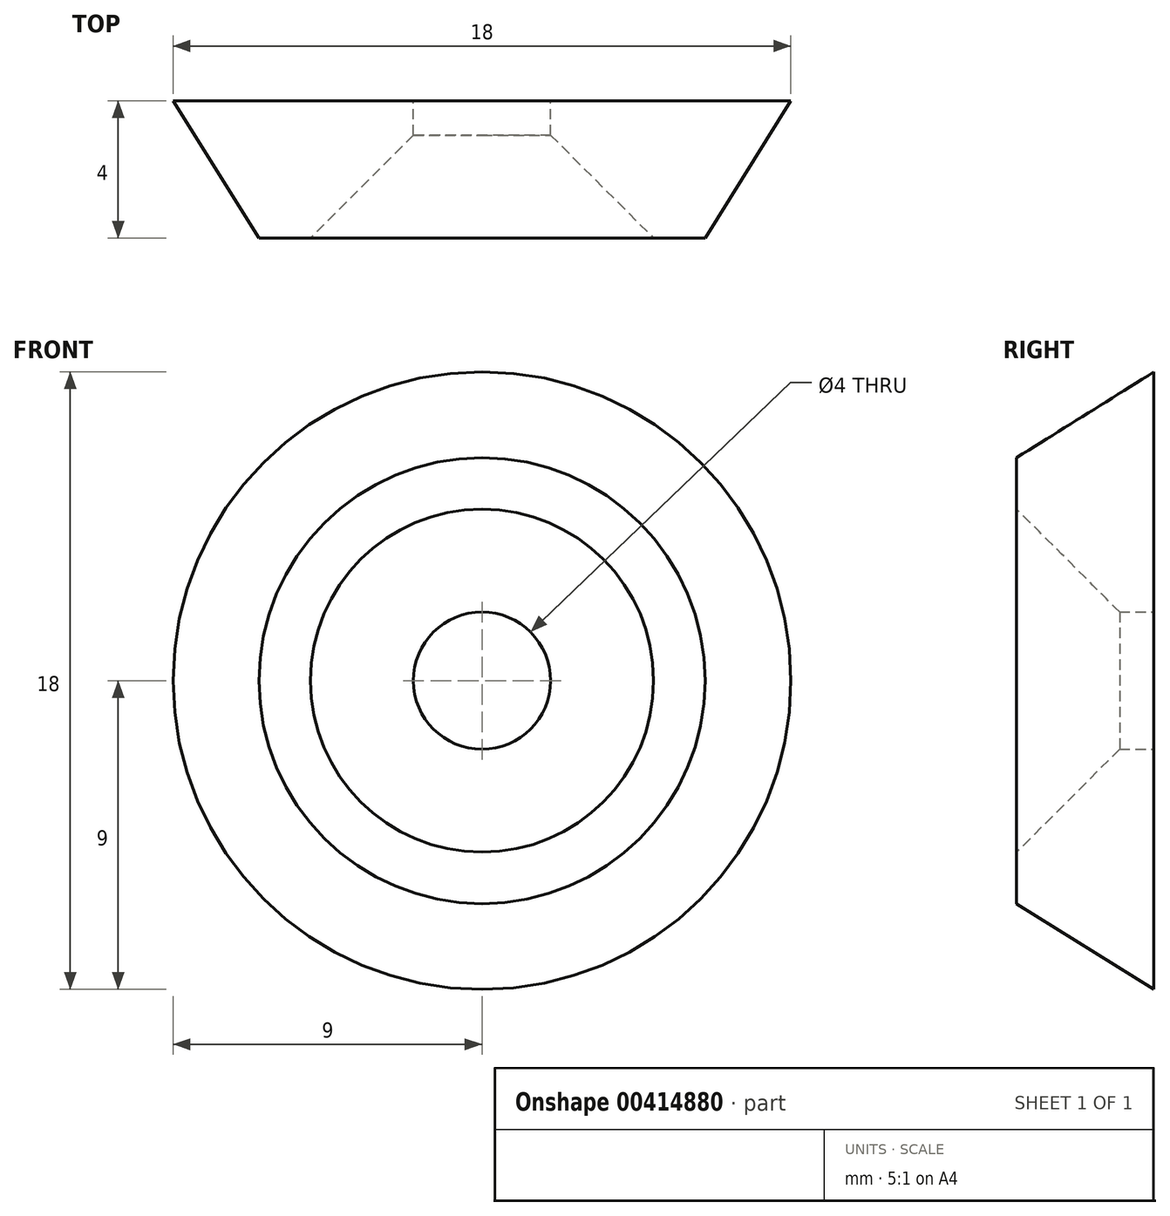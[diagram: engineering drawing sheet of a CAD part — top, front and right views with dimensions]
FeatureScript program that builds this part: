
annotation { "Feature Type Name" : "Feature", "Feature Type Description" : "" }
export const myFeature = defineFeature(function(context is Context, id is Id, definition is map)
    precondition{}
    {
        {
            var Q0;
            Q0=qCreatedBy(makeId("Right.planeOp"),FACE);
            var sketch = newSketch(context, id + "F0", { "sketchPlane" : qUnion([Q0])});
            skLineSegment(sketch, "E0", {"start": v(0, 0) * mm, "end": v(-4, 0) * mm, "construction": true});
            skLineSegment(sketch, "E1", {"start": v(0, 2) * mm, "end": v(0, 9) * mm});
            skLineSegment(sketch, "E2", {"start": v(0, 9) * mm, "end": v(-4, 6.5) * mm});
            skLineSegment(sketch, "E3", {"start": v(-4, 6.5) * mm, "end": v(-4, 5) * mm});
            skLineSegment(sketch, "E4", {"start": v(-4, 5) * mm, "end": v(-1, 2) * mm});
            skLineSegment(sketch, "E5", {"start": v(-1, 2) * mm, "end": v(0, 2) * mm});
            skLineSegment(sketch, "E6", {"start": v(-4, 5) * mm, "end": v(-4, 0) * mm, "construction": true});
            skSolve(sketch);
        }
        {
            var Q0;
            Q0=makeQuery(id+"F0.imprint","IMPRINT",FACE,{"disambiguationData":[TD([[makeQuery(id+"F0.imprint","IMPRINT",EDGE,{"derivedFrom":sQuery(id+"F0.wireOp",EDGE,"E1")}),1.0]])]});
            var Q1;
            Q1=sQuery(id+"F0.wireOp",EDGE,"E0");
            revolve(context, id + "F1", {"entities" : qUnion([Q0]), "axis" : qUnion([Q1]), "revolveType" : RevolveType.FULL});
        }
    });
